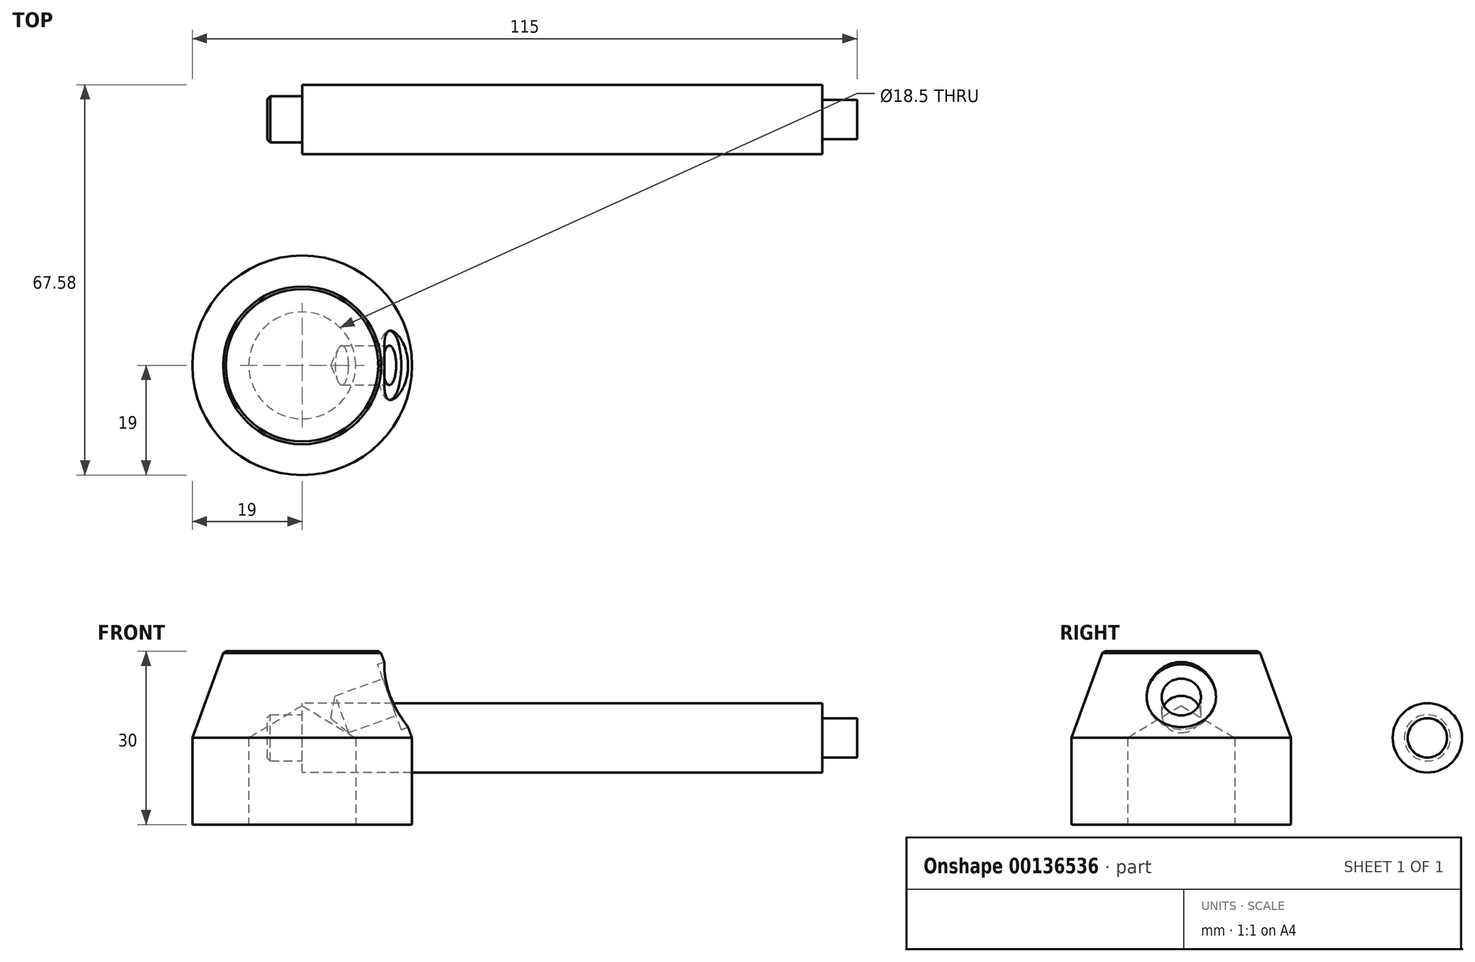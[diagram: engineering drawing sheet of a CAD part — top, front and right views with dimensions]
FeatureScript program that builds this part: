
annotation { "Feature Type Name" : "Feature", "Feature Type Description" : "" }
export const myFeature = defineFeature(function(context is Context, id is Id, definition is map)
    precondition{}
    {
        {
            var Q0;
            Q0=qCreatedBy(makeId("Top.planeOp"),FACE);
            var sketch = newSketch(context, id + "F0", { "sketchPlane" : qUnion([Q0])});
            skCircle(sketch, "E0", {"center": v(0, 0) * mm, "radius": 19 * mm});
            skSolve(sketch);
        }
        {
            var Q0;
            Q0=makeQuery(id+"F0.imprint","IMPRINT",FACE,{"disambiguationData":[TD([[makeQuery(id+"F0.imprint","IMPRINT",EDGE,{"derivedFrom":sQuery(id+"F0.wireOp",EDGE,"E0")}),1.0]])]});
            extrude(context, id + "F1", {"entities" : qUnion([Q0]), "depth" : 15 * mm, "hasDraft" : true, "draftAngle" : 20 * degree, "draftPullDirection" : true});
        }
        {
            var Q0;
            Q0=makeQuery(id+"F1.opExtrude","CAP_FACE",FACE,{"disambiguationData":[OSD([sQuery(id+"F0.wireOp",EDGE,"E0")])],"isStart":true});
            extrude(context, id + "F2", {"entities" : qUnion([Q0]), "operationType" : NewBodyOperationType.ADD, "depth" : 15 * mm});
        }
        {
            var Q0;
            Q0=qCreatedBy(makeId("Front.planeOp"),FACE);
            var sketch = newSketch(context, id + "F3", { "sketchPlane" : qUnion([Q0])});
            skLineSegment(sketch, "E1", {"start": v(13.54, 15) * mm, "end": v(19, 0) * mm, "construction": true});
            skPoint(sketch, "E2", {"position": v(13.54, 15) * mm});
            skPoint(sketch, "E3", {"position": v(19, 0) * mm});
            skLineSegment(sketch, "E4", {"start": v(16.27, 7.5) * mm, "end": v(25.9, 11.77) * mm, "construction": true});
            skSolve(sketch);
        }
        {
            var Q0;
            Q0=makeQuery(id+"F1.opExtrude","CAP_EDGE",EDGE,{"disambiguationData":[OSD([sQuery(id+"F0.wireOp",EDGE,"E0")])],"isStart":false});
            chamfer(context, id + "F4", {"entities" : qUnion([Q0]), "width" : .5 * mm, "tangentPropagation" : true});
        }
        {
            var Q0;
            Q0=sQuery(id+"F3.wireOp",EDGE,"E1");
            cPlane(context, id + "F5", {"entities" : qUnion([Q0]), "cplaneType" : CPlaneType.LINE_ANGLE, "offset" : 25 * mm, "angle" : 0 * degree, "width" : 150 * mm, "height" : 150 * mm});
        }
        {
            var Q0;
            Q0=qCreatedBy(id+"F5.planeOp",FACE);
            var sketch = newSketch(context, id + "F6", { "sketchPlane" : qUnion([Q0])});
            skPoint(sketch, "E5", {"position": v(0, 1.48) * mm});
            skCircle(sketch, "E6", {"center": v(0, 1.48) * mm, "radius": 6 * mm});
            skSolve(sketch);
        }
        {
            var Q0;
            Q0 = qSketchRegion(id + "F6", true);
            extrude(context, id + "F7", {"entities" : qUnion([Q0]), "operationType" : NewBodyOperationType.REMOVE, "depth" : 1.25 * mm});
        }
        {
            var Q0;
            Q0=sQuery(id+"F6.wireOp",VERTEX,"E5");
            var Q1;
            Q1=makeQuery(id+"F1.opExtrude","SWEPT_BODY",BODY,{"disambiguationData":[OSD([sQuery(id+"F0.wireOp",EDGE,"E0")])]});
            hole(context, id + "F8", {"style" : HoleStyle.SIMPLE, "endStyle" : HoleEndStyle.BLIND, "oppositeDirection" : true, "standardTappedOrClearance" : lookupTablePath({ "standard" : "ISO", "engagement" : "75%", "pitch" : "1.25 mm", "size" : "M8", "type" : "Tapped" }), "standardBlindInLast" : lookupTablePath({ "standard" : "ISO", "engagement" : "75%", "pitch" : "1.25 mm", "size" : "M8", "type" : "Tapped" }), "holeDiameter" : 6.8 * mm, "showTappedDepth" : true, "holeDepth" : 10 * mm, "tappedDepth" : 6.25 * mm, "tapClearance" : 3, "startFromSketch" : true, "locations" : qUnion([Q0]), "scope" : qUnion([Q1]), "majorDiameter" : 8 * mm});
        }
        {
            var Q0;
            Q0=makeQuery(id+"F2.opExtrude","CAP_FACE",FACE,{"disambiguationData":[OSD([sQuery(id+"F0.wireOp",EDGE,"E0")])],"isStart":false});
            var sketch = newSketch(context, id + "F9", { "sketchPlane" : qUnion([Q0])});
            skPoint(sketch, "E7", {"position": v(0, 0) * mm});
            skSolve(sketch);
        }
        {
            var Q0;
            Q0=sQuery(id+"F9.wireOp",VERTEX,"E7");
            var Q1;
            Q1=makeQuery(id+"F1.opExtrude","SWEPT_BODY",BODY,{"disambiguationData":[OSD([sQuery(id+"F0.wireOp",EDGE,"E0")])]});
            hole(context, id + "F10", {"style" : HoleStyle.SIMPLE, "endStyle" : HoleEndStyle.BLIND, "standardTappedOrClearance" : lookupTablePath({ "standard" : "ISO", "engagement" : "75%", "pitch" : "1.5 mm", "size" : "M20", "type" : "Tapped" }), "standardBlindInLast" : lookupTablePath({ "standard" : "ISO", "engagement" : "75%", "pitch" : "1.5 mm", "size" : "M20", "type" : "Tapped" }), "holeDiameter" : 18.5 * mm, "showTappedDepth" : true, "holeDepth" : 15 * mm, "tappedDepth" : 10.5 * mm, "tapClearance" : 3, "startFromSketch" : true, "locations" : qUnion([Q0]), "scope" : qUnion([Q1]), "majorDiameter" : 20 * mm});
        }
        {
            var Q0;
            Q0=qCreatedBy(makeId("Right.planeOp"),FACE);
            var sketch = newSketch(context, id + "F11", { "sketchPlane" : qUnion([Q0])});
            skCircle(sketch, "E8", {"center": v(42.58, 0) * mm, "radius": 4 * mm});
            skCircle(sketch, "E9", {"center": v(42.58, 0) * mm, "radius": 6 * mm});
            skSolve(sketch);
        }
        {
            var Q0;
            Q0=makeQuery(id+"F11.imprint","IMPRINT",FACE,{"disambiguationData":[TD([[makeQuery(id+"F11.imprint","IMPRINT",EDGE,{"derivedFrom":sQuery(id+"F11.wireOp",EDGE,"E8")}),1.0]])]});
            extrude(context, id + "F12", {"entities" : qUnion([Q0]), "oppositeDirection" : true, "depth" : 6 * mm});
        }
        {
            var Q0;
            Q0 = qSketchRegion(id + "F11", true);
            var Q1;
            Q1=makeQuery(id+"F12.opExtrude","CAP_FACE",FACE,{"disambiguationData":[OSD([sQuery(id+"F11.wireOp",EDGE,"E8")])],"isStart":true});
            extrude(context, id + "F13", {"entities" : qUnion([Q0, Q1]), "operationType" : NewBodyOperationType.ADD, "depth" : 90 * mm});
        }
        {
            var Q0;
            Q0=makeQuery(id+"F12.opExtrude","CAP_EDGE",EDGE,{"disambiguationData":[OSD([sQuery(id+"F11.wireOp",EDGE,"E8")])],"isStart":false});
            chamfer(context, id + "F14", {"entities" : qUnion([Q0]), "width" : .5 * mm, "tangentPropagation" : true});
        }
        {
            var Q0;
            {var subQ0=sQuery(id+"F11.wireOp",EDGE,"E8");Q0=makeQuery(id+"F13.boolean.opBoolean","MERGE",FACE,{"derivedFrom":[makeQuery(id+"F13.opExtrude","CAP_FACE",FACE,{"disambiguationData":[OSD([subQ0,sQuery(id+"F11.wireOp",EDGE,"E9")])],"isStart":false}),makeQuery(id+"F13.opExtrude","CAP_FACE",FACE,{"disambiguationData":[OSD([subQ0])],"isStart":false})]});}
            var sketch = newSketch(context, id + "F15", { "sketchPlane" : qUnion([Q0])});
            skCircle(sketch, "E10", {"center": v(42.58, 0) * mm, "radius": 3.4 * mm});
            skSolve(sketch);
        }
        {
            var Q0;
            Q0=makeQuery(id+"F15.imprint","IMPRINT",FACE,{"disambiguationData":[TD([[makeQuery(id+"F15.imprint","IMPRINT",EDGE,{"derivedFrom":sQuery(id+"F15.wireOp",EDGE,"E10")}),1.0]])]});
            extrude(context, id + "F16", {"entities" : qUnion([Q0]), "operationType" : NewBodyOperationType.ADD, "depth" : 6 * mm});
        }
        {
            var Q0;
            Q0=qCreatedBy(makeId("Right.planeOp"),FACE);
            var sketch = newSketch(context, id + "F17", { "sketchPlane" : qUnion([Q0])});
            skArc(sketch, "E11", {"start": v(92.49, -19) * mm, "mid": v(111.49, 0) * mm, "end": v(92.49, 19) * mm});
            skLineSegment(sketch, "E12", {"start": v(92.49, 19) * mm, "end": v(92.49, -19) * mm, "construction": true});
            skLineSegment(sketch, "E13", {"start": v(92.49, 0) * mm, "end": v(111.49, 0) * mm, "construction": true});
            skSolve(sketch);
        }
        {
            var Q0;
            Q0=sQuery(id+"F17.wireOp",EDGE,"E11");
            var Q1;
            Q1=sQuery(id+"F17.wireOp",EDGE,"E12");
            revolve(context, id + "F18", {"bodyType" : ToolBodyType.SURFACE, "surfaceEntities" : qUnion([Q0]), "axis" : qUnion([Q1]), "revolveType" : RevolveType.FULL});
        }
    });
